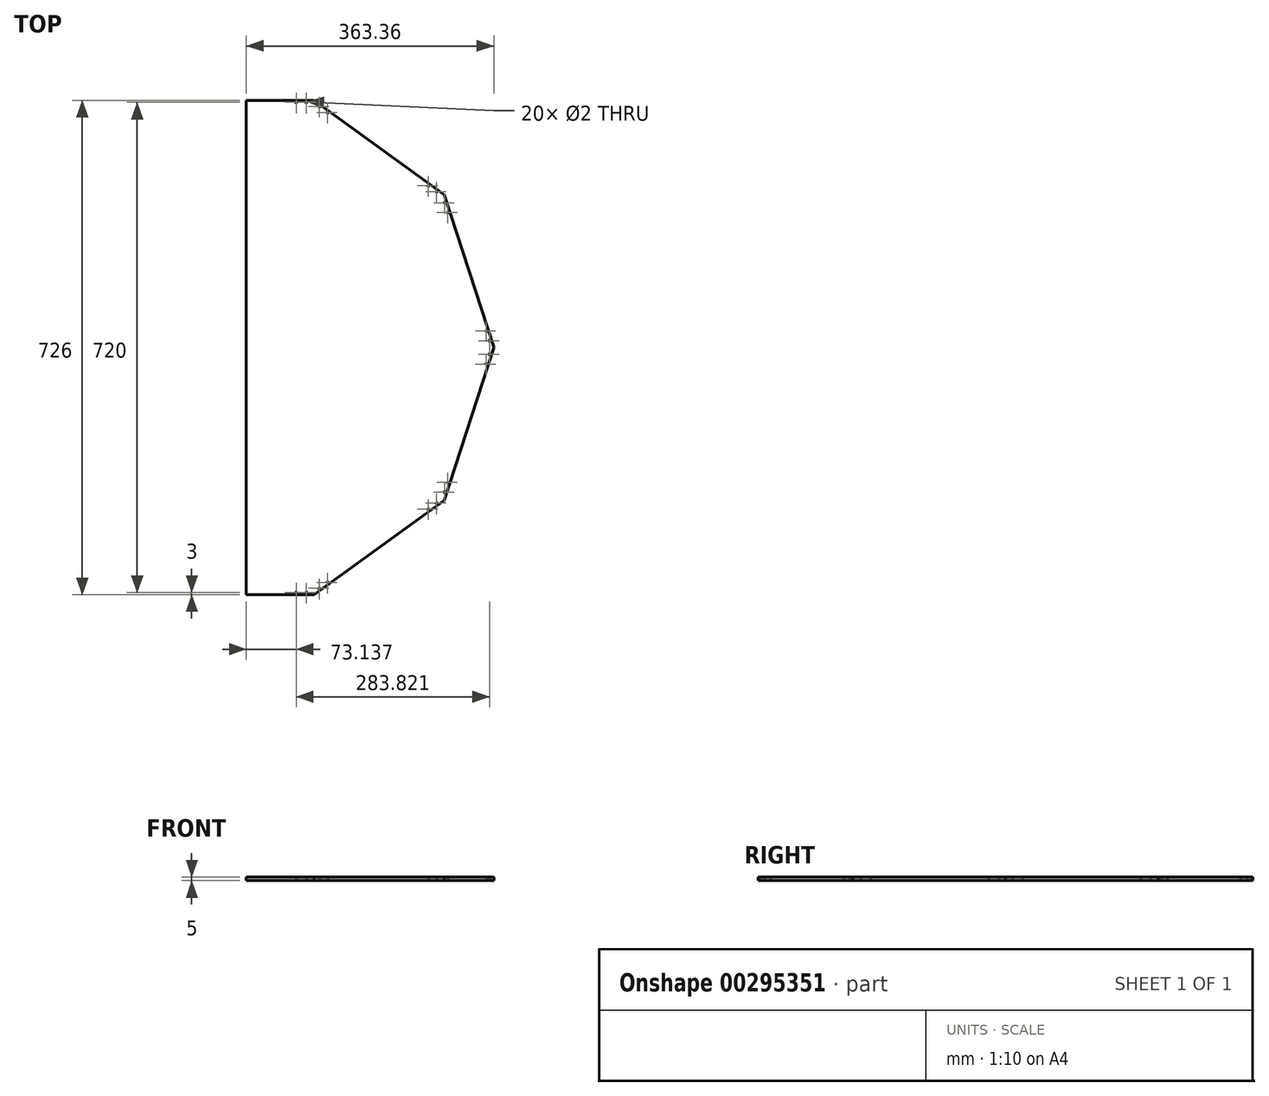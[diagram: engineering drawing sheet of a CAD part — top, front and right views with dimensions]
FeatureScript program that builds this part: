
annotation { "Feature Type Name" : "Feature", "Feature Type Description" : "" }
export const myFeature = defineFeature(function(context is Context, id is Id, definition is map)
    precondition{}
    {
        {
            var Q0;
            Q0=qCreatedBy(makeId("Top.planeOp"),FACE);
            var sketch = newSketch(context, id + "F0", { "sketchPlane" : qUnion([Q0])});
            skCircle(sketch, "E0", {"center": v(375.28, 10) * mm, "radius": 1 * mm});
            skCircle(sketch, "E1", {"center": v(370.64, 24.27) * mm, "radius": 1 * mm});
            skLineSegment(sketch, "E2", {"start": v(18.32, 363) * mm, "end": v(18.32, -363) * mm});
            skLineSegment(sketch, "E3.0", {"start": v(381.68, 0) * mm, "end": v(308.79, -224.35) * mm});
            skLineSegment(sketch, "E3.1", {"start": v(308.79, -224.35) * mm, "end": v(117.95, -363) * mm});
            skLineSegment(sketch, "E3.2", {"start": v(117.95, -363) * mm, "end": v(18.32, -363) * mm});
            skLineSegment(sketch, "E3.7", {"start": v(18.32, 363) * mm, "end": v(117.95, 363) * mm});
            skLineSegment(sketch, "E3.8", {"start": v(117.95, 363) * mm, "end": v(308.79, 224.35) * mm});
            skLineSegment(sketch, "E3.9", {"start": v(308.79, 224.35) * mm, "end": v(381.68, 0) * mm});
            skCircle(sketch, "E4.1.1", {"center": v(297.73, 228.67) * mm, "radius": 1 * mm});
            skCircle(sketch, "E4.1.3", {"center": v(285.6, 237.49) * mm, "radius": 1 * mm});
            skCircle(sketch, "E4.2.1", {"center": v(106.46, 360) * mm, "radius": 1 * mm});
            skCircle(sketch, "E4.2.3", {"center": v(91.46, 360) * mm, "radius": 1 * mm});
            skCircle(sketch, "E4.8.1", {"center": v(125.48, -353.82) * mm, "radius": 1 * mm});
            skCircle(sketch, "E4.8.3", {"center": v(137.61, -345) * mm, "radius": 1 * mm});
            skCircle(sketch, "E4.9.1", {"center": v(309.48, -212.5) * mm, "radius": 1 * mm});
            skCircle(sketch, "E4.9.3", {"center": v(314.12, -198.23) * mm, "radius": 1 * mm});
            skCircle(sketch, "E5", {"center": v(125.48, 353.82) * mm, "radius": 1 * mm});
            skCircle(sketch, "E6", {"center": v(137.61, 345) * mm, "radius": 1 * mm});
            skCircle(sketch, "E7", {"center": v(309.48, 212.5) * mm, "radius": 1 * mm});
            skCircle(sketch, "E8", {"center": v(314.12, 198.23) * mm, "radius": 1 * mm});
            skCircle(sketch, "E9", {"center": v(375.28, -10) * mm, "radius": 1 * mm});
            skCircle(sketch, "E10", {"center": v(370.64, -24.27) * mm, "radius": 1 * mm});
            skCircle(sketch, "E11", {"center": v(297.73, -228.67) * mm, "radius": 1 * mm});
            skCircle(sketch, "E12", {"center": v(285.6, -237.49) * mm, "radius": 1 * mm});
            skCircle(sketch, "E13", {"center": v(91.46, -360) * mm, "radius": 1 * mm});
            skCircle(sketch, "E14", {"center": v(106.46, -360) * mm, "radius": 1 * mm});
            skLineSegment(sketch, "E15.bottom", {"start": v(383.94, -254.94) * mm, "end": v(383.94, 195.06) * mm});
            skLineSegment(sketch, "E15.top", {"start": v(393.94, -254.94) * mm, "end": v(393.94, 195.06) * mm});
            skLineSegment(sketch, "E15.left", {"start": v(383.94, -254.94) * mm, "end": v(393.94, -254.94) * mm});
            skLineSegment(sketch, "E15.right", {"start": v(383.94, 195.06) * mm, "end": v(393.94, 195.06) * mm});
            skPoint(sketch, "E15.middle", {"position": v(388.94, -29.94) * mm});
            skCircle(sketch, "E16", {"center": v(388.94, 190.06) * mm, "radius": 2.5 * mm});
            skLineSegment(sketch, "E17.bottom", {"start": v(386.44, -249.94) * mm, "end": v(386.44, -134.94) * mm});
            skLineSegment(sketch, "E17.top", {"start": v(391.44, -249.94) * mm, "end": v(391.44, -134.94) * mm});
            skLineSegment(sketch, "E17.left", {"start": v(386.44, -249.94) * mm, "end": v(391.44, -249.94) * mm});
            skLineSegment(sketch, "E17.right", {"start": v(386.44, -134.94) * mm, "end": v(391.44, -134.94) * mm});
            skPoint(sketch, "E17.middle", {"position": v(388.94, -192.44) * mm});
            skCircle(sketch, "E18", {"center": v(388.94, 0.06) * mm, "radius": 2.5 * mm});
            skLineSegment(sketch, "E19.bottom", {"start": v(374.99, -205.7) * mm, "end": v(374.99, -355.7) * mm});
            skLineSegment(sketch, "E19.top", {"start": v(364.99, -205.7) * mm, "end": v(364.99, -355.7) * mm});
            skLineSegment(sketch, "E19.left", {"start": v(374.99, -205.7) * mm, "end": v(364.99, -205.7) * mm});
            skLineSegment(sketch, "E19.right", {"start": v(374.99, -355.7) * mm, "end": v(364.99, -355.7) * mm});
            skPoint(sketch, "E19.middle", {"position": v(369.99, -280.7) * mm});
            skCircle(sketch, "E20", {"center": v(369.99, -350.7) * mm, "radius": 2.5 * mm});
            skCircle(sketch, "E21", {"center": v(347.4, -352.37) * mm, "radius": 2.5 * mm});
            skCircle(sketch, "E22", {"center": v(347.4, -287.37) * mm, "radius": 2.5 * mm});
            skLineSegment(sketch, "E23.bottom", {"start": v(352.4, -282.37) * mm, "end": v(352.4, -357.37) * mm});
            skLineSegment(sketch, "E23.top", {"start": v(342.4, -282.37) * mm, "end": v(342.4, -357.37) * mm});
            skLineSegment(sketch, "E23.left", {"start": v(352.4, -282.37) * mm, "end": v(342.4, -282.37) * mm});
            skLineSegment(sketch, "E23.right", {"start": v(352.4, -357.37) * mm, "end": v(342.4, -357.37) * mm});
            skPoint(sketch, "E23.middle", {"position": v(347.4, -319.87) * mm});
            skCircle(sketch, "E24", {"center": v(369.99, -210.7) * mm, "radius": 2.5 * mm});
            skSolve(sketch);
        }
        {
            var Q0;
            Q0=makeQuery(id+"F0.imprint","IMPRINT",FACE,{"disambiguationData":[TD([[makeQuery(id+"F0.imprint","IMPRINT",EDGE,{"derivedFrom":sQuery(id+"F0.wireOp",EDGE,"E0")}),-1.0]])]});
            extrude(context, id + "F1", {"entities" : qUnion([Q0]), "depth" : 5 * mm});
        }
    });
